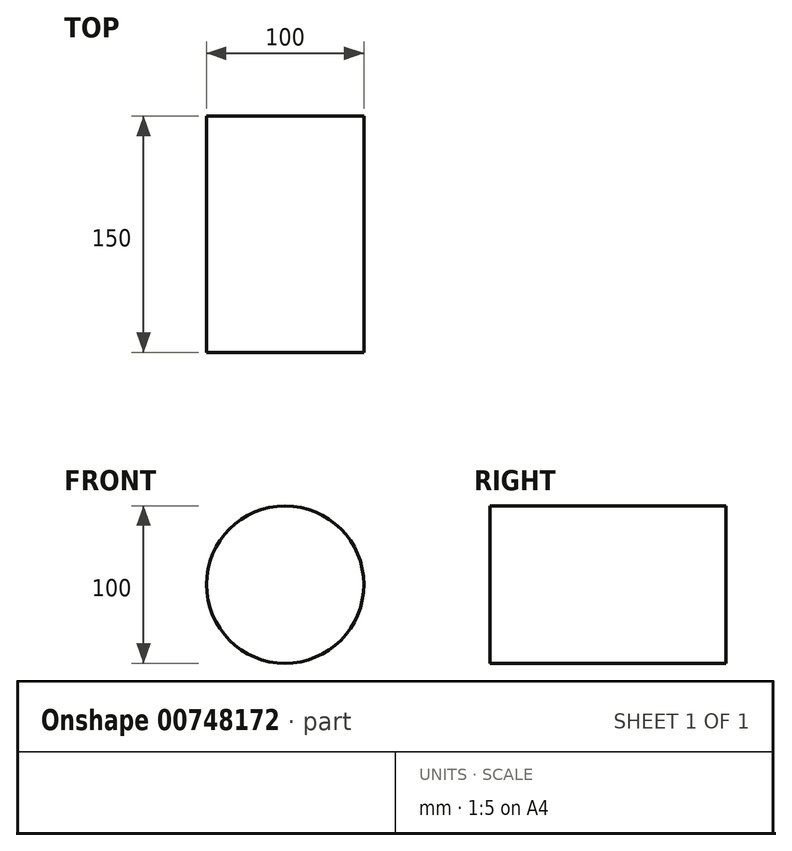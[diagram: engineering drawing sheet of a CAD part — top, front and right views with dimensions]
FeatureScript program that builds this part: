
annotation { "Feature Type Name" : "Feature", "Feature Type Description" : "" }
export const myFeature = defineFeature(function(context is Context, id is Id, definition is map)
    precondition{}
    {
        {
            var Q0;
            Q0=qCreatedBy(makeId("Front.planeOp"),FACE);
            var sketch = newSketch(context, id + "F0", { "sketchPlane" : qUnion([Q0])});
            skCircle(sketch, "E0", {"center": v(0, 0) * mm, "radius": 50 * mm});
            skSolve(sketch);
        }
        {
            var Q0;
            Q0 = qSketchRegion(id + "F0", true);
            extrude(context, id + "F1", {"entities" : qUnion([Q0]), "depth" : 150 * mm, "offsetDistance" : 25 * mm});
        }
    });
